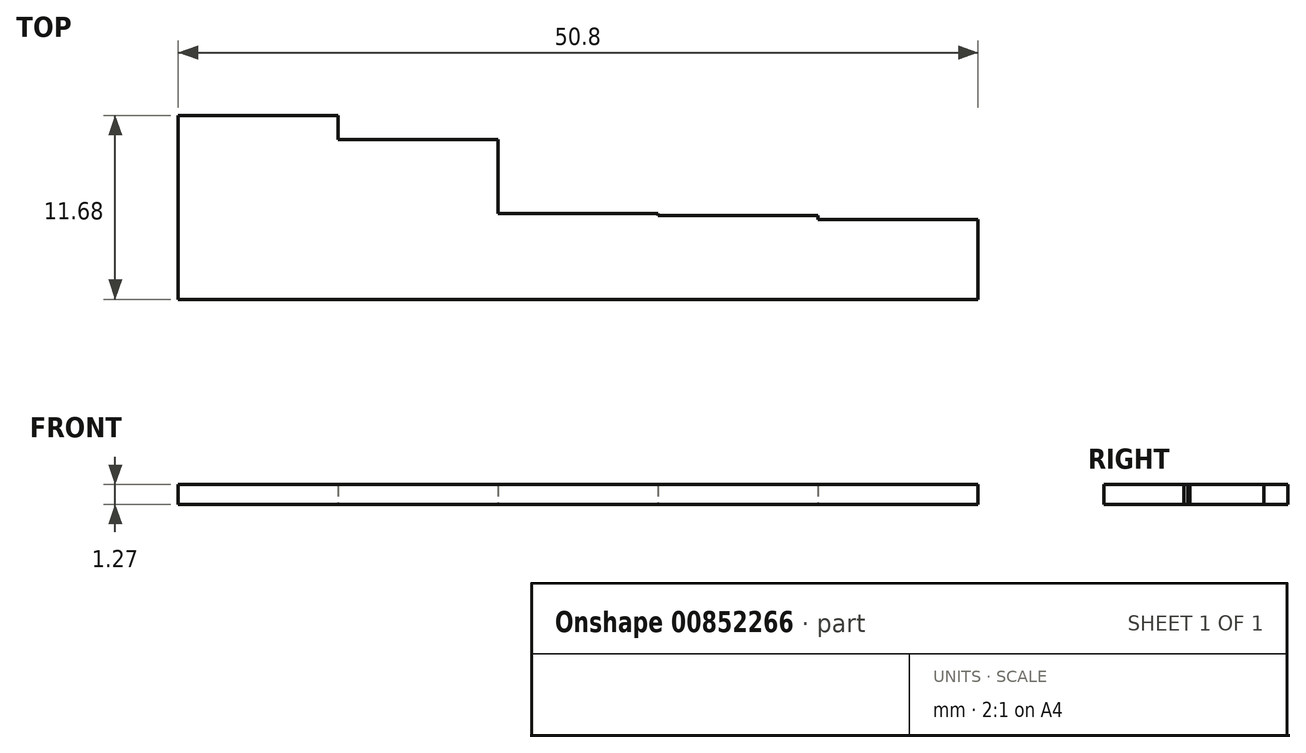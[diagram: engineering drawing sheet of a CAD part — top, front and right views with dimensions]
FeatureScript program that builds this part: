
annotation { "Feature Type Name" : "Feature", "Feature Type Description" : "" }
export const myFeature = defineFeature(function(context is Context, id is Id, definition is map)
    precondition{}
    {
        {
            var Q0;
            Q0=qCreatedBy(makeId("Top.planeOp"),FACE);
            var sketch = newSketch(context, id + "F0", { "sketchPlane" : qUnion([Q0])});
            skLineSegment(sketch, "E0", {"start": v(0, 0) * mm, "end": v(50.8, 0) * mm});
            skLineSegment(sketch, "E1", {"start": v(50.8, 0) * mm, "end": v(50.8, 5.08) * mm});
            skLineSegment(sketch, "E2", {"start": v(50.8, 5.08) * mm, "end": v(40.64, 5.08) * mm});
            skLineSegment(sketch, "E3", {"start": v(40.64, 5.08) * mm, "end": v(40.64, 5.33) * mm});
            skLineSegment(sketch, "E4", {"start": v(40.64, 5.33) * mm, "end": v(30.48, 5.33) * mm});
            skLineSegment(sketch, "E5", {"start": v(30.48, 5.33) * mm, "end": v(30.48, 5.46) * mm});
            skLineSegment(sketch, "E6", {"start": v(30.48, 5.46) * mm, "end": v(20.32, 5.46) * mm});
            skLineSegment(sketch, "E7", {"start": v(20.32, 5.46) * mm, "end": v(20.32, 10.16) * mm});
            skLineSegment(sketch, "E8", {"start": v(20.32, 10.16) * mm, "end": v(10.16, 10.16) * mm});
            skLineSegment(sketch, "E9", {"start": v(10.16, 10.16) * mm, "end": v(10.16, 11.68) * mm});
            skLineSegment(sketch, "E10", {"start": v(10.16, 11.68) * mm, "end": v(0, 11.68) * mm});
            skLineSegment(sketch, "E11", {"start": v(0, 11.68) * mm, "end": v(0, 0) * mm});
            skSolve(sketch);
        }
        {
            var Q0;
            Q0=makeQuery(id+"F0.imprint","IMPRINT",FACE,{"disambiguationData":[TD([[makeQuery(id+"F0.imprint","IMPRINT",EDGE,{"derivedFrom":sQuery(id+"F0.wireOp",EDGE,"E0")}),1.0]])]});
            extrude(context, id + "F1", {"entities" : qUnion([Q0]), "depth" : 1.27 * mm, "offsetDistance" : 25.4 * mm});
        }
    });
